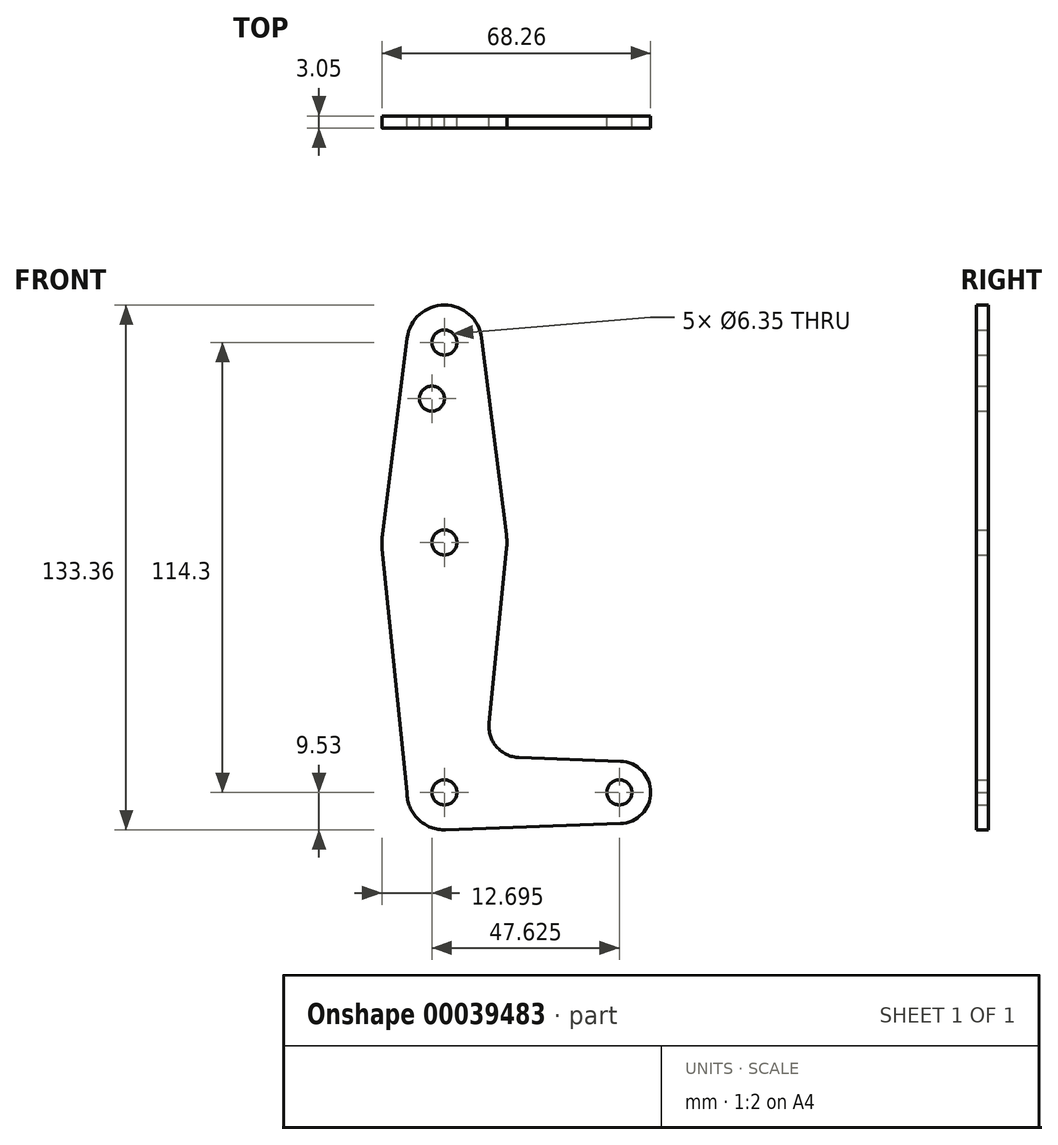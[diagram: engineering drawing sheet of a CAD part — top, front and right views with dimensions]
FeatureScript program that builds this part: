
annotation { "Feature Type Name" : "Feature", "Feature Type Description" : "" }
export const myFeature = defineFeature(function(context is Context, id is Id, definition is map)
    precondition{}
    {
        {
            var Q0;
            Q0=qCreatedBy(makeId("Front.planeOp"),FACE);
            var sketch = newSketch(context, id + "F0", { "sketchPlane" : qUnion([Q0])});
            skLineSegment(sketch, "E0", {"start": v(0, 0) * mm, "end": v(0, 114.3) * mm, "construction": true});
            skLineSegment(sketch, "E1", {"start": v(0, 0) * mm, "end": v(44.45, 0) * mm, "construction": true});
            skCircle(sketch, "E2", {"center": v(0, 114.3) * mm, "radius": 9.52 * mm});
            skCircle(sketch, "E3", {"center": v(0, 0) * mm, "radius": 9.52 * mm});
            skCircle(sketch, "E4", {"center": v(44.45, 0) * mm, "radius": 7.94 * mm});
            skCircle(sketch, "E5", {"center": v(0, 63.5) * mm, "radius": 15.88 * mm});
            skLineSegment(sketch, "E6", {"start": v(-9.45, 115.5) * mm, "end": v(-15.75, 65.48) * mm});
            skLineSegment(sketch, "E7", {"start": v(-15.8, 61.9) * mm, "end": v(-9.52, 0) * mm});
            skLineSegment(sketch, "E8", {"start": v(9.45, 115.5) * mm, "end": v(15.75, 65.48) * mm});
            skLineSegment(sketch, "E9", {"start": v(11.34, 17.6) * mm, "end": v(15.8, 61.91) * mm});
            skLineSegment(sketch, "E10", {"start": v(18.97, 8.85) * mm, "end": v(44.73, 7.93) * mm});
            skLineSegment(sketch, "E11", {"start": v(0.34, -9.52) * mm, "end": v(44.73, -7.93) * mm});
            skCircle(sketch, "E12", {"center": v(0, 114.3) * mm, "radius": 3.18 * mm});
            skCircle(sketch, "E13", {"center": v(0, 63.5) * mm, "radius": 3.18 * mm});
            skCircle(sketch, "E14", {"center": v(0, 0) * mm, "radius": 3.18 * mm});
            skCircle(sketch, "E15", {"center": v(44.45, 0) * mm, "radius": 3.18 * mm});
            skCircle(sketch, "E16", {"center": v(-3.18, 100.03) * mm, "radius": 3.18 * mm});
            skArc(sketch, "E17.filletArc", {"start": v(11.34, 17.6) * mm, "mid": v(13.26, 11.57) * mm, "end": v(18.97, 8.85) * mm});
            skSolve(sketch);
        }
        {
            var Q0;
            Q0 = qSketchRegion(id + "F0", true);
            extrude(context, id + "F1", {"entities" : qUnion([Q0]), "depth" : 3.05 * mm});
        }
    });
